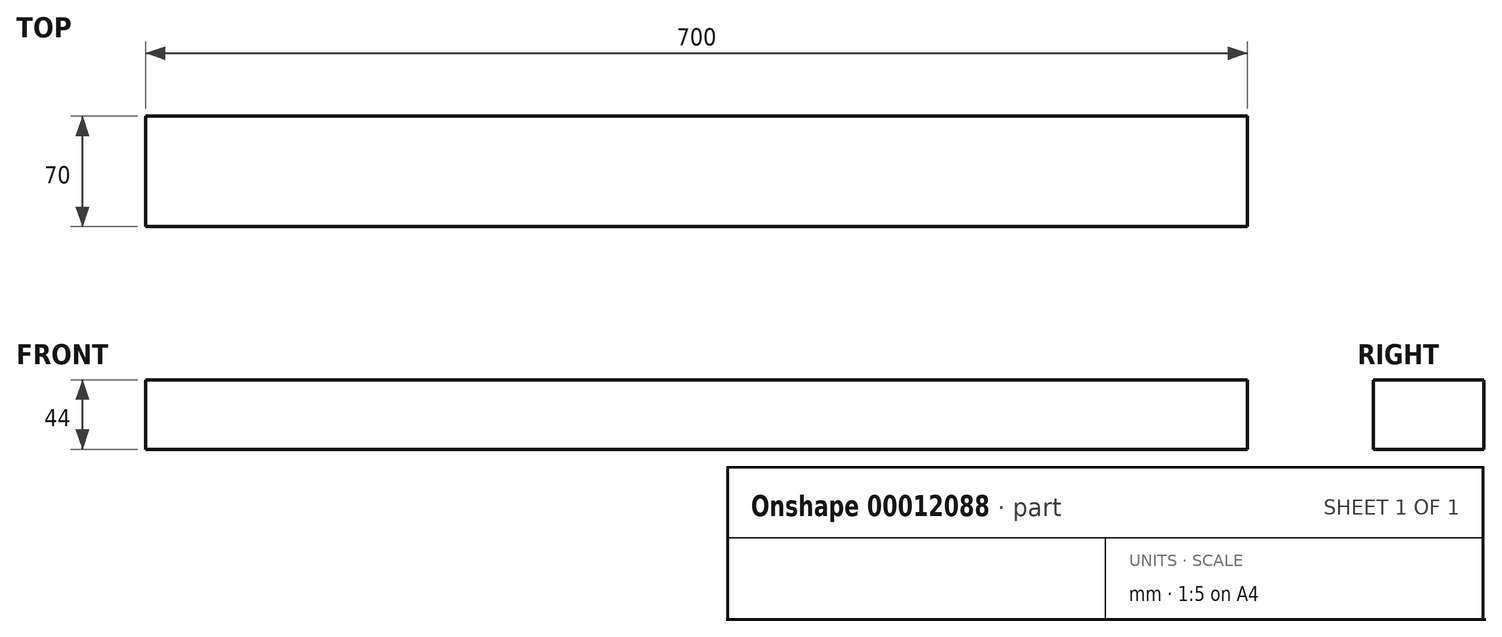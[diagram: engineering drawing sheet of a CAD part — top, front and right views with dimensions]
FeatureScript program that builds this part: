
annotation { "Feature Type Name" : "Feature", "Feature Type Description" : "" }
export const myFeature = defineFeature(function(context is Context, id is Id, definition is map)
    precondition{}
    {
        {
            var Q0;
            Q0=qCreatedBy(makeId("Right.planeOp"),FACE);
            var sketch = newSketch(context, id + "F0", { "sketchPlane" : qUnion([Q0])});
            skLineSegment(sketch, "E0.bottom", {"start": v(0, 0) * mm, "end": v(-70, 0) * mm});
            skLineSegment(sketch, "E0.top", {"start": v(0, 44) * mm, "end": v(-70, 44) * mm});
            skLineSegment(sketch, "E0.left", {"start": v(0, 0) * mm, "end": v(0, 44) * mm});
            skLineSegment(sketch, "E0.right", {"start": v(-70, 0) * mm, "end": v(-70, 44) * mm});
            skSolve(sketch);
        }
        {
            var Q0;
            Q0 = qSketchRegion(id + "F0", true);
            extrude(context, id + "F1", {"entities" : qUnion([Q0]), "depth" : 700 * mm, "symmetric" : true});
        }
    });
